# Revit family: Faucet-Lavatory-KOHLER-ARTIFACTS-K-76031T
name_source: partatom
category: Plumbing Fixtures
revit_build: Autodesk Revit 2017 (Build: 20160225_1515(x64)
units: mm (PartAtom-declared; Revit-internal decimal feet)

## family parameters
Cut with Voids When Loaded = No
Host = Face
OmniClass Number = 23.31.11.00
OmniClass Title = Faucets
Part Type = Normal
Room Calculation Point = No
Round Connector Dimension = Use Diameter
Shared = No

## types (10) — shared parameters
ADA Compliant = No
Assembly Code = D2010
CW Connection = Yes
Cold Water Inlet = Cold Water Inlet
Date Modified = 09/23/2020
Default Elevation = 36"
Description = 8  Basin Faucet-Curved spout with wing handle
Drain Included = Yes
Flow Rate = 2 GPM
HW Connection = Yes
Handle Clearance = 2 3/4"
Height = 4 11/16"
Hot Water Inlet = Hot Water Inlet
Length = 7 3/16"
Manufacturer = KOHLER Co.
Master Format 2014 = 22 41 39
Master Format 2014 Name = Residential Faucets, Supplies, and Trim
Material = Premium Metal Construction
Pressure = 60.00 psi
Product Documentation Link = https://files.kohler.com.cn
Product Name = ARTIFACTS
Product Page URL = https://www.kohler.com.cn
Spout Reach = 5 3/8"
URL = http://www.kohler.com.cn
Vent Connection = No
Waste Connection = No
Waste Water Outlet = Waste Water Outlet
WaterSense Certified = No

## per-type parameters (varying)
| type | Finish | Model | Type |
| CP- Polished Chrome | Kohler-Metal-CP-Polished_Chrome | K-76031T-9M-CP | 1 |
| BV- Roman Copper | Kohler-Metal-BV-Roman_Copper | K-76031T-9M-BV | 2 |
| RGD-Rose Gold | Kohler-Metal-RGD-Rose_Gold | K-76031T-9M-RGD | 3 |
| 2BZ-Elegant Black | Kohler-Metal-2BZ-Elegant_Black | K-76031T-9M-2BZ | 4 |
| AF-Flange Gold | Kohler-Metal-AF-Flange_Gold | K-76031T-9M-AF | 5 |
| BN-Roman Silver | Kohler-Metal-BN-Roman_Silver | K-76031T-9M-BN | 6 |
| SN-Champagne Gold | Kohler-Metal-SN-Champagne_Gold | K-76031T-9M-SN | 7 |
| PGD-Eternal Gold | Kohler-Metal-PGD-Eternal_Gold | K-76031T-9M-PGD | 8 |
| TT-Titanium Silver | Kohler-Metal-TT-Titanium_Silver | K-76031T-9M-TT | 9 |
| 2BL-Original Black | Kohler-Metal-2BL-Original_Black | K-76031T-9M-2BL | 10 |

## geometry (parser evidence)
native form markers: Sweep x10
no freeform markers — native parametric forms only
